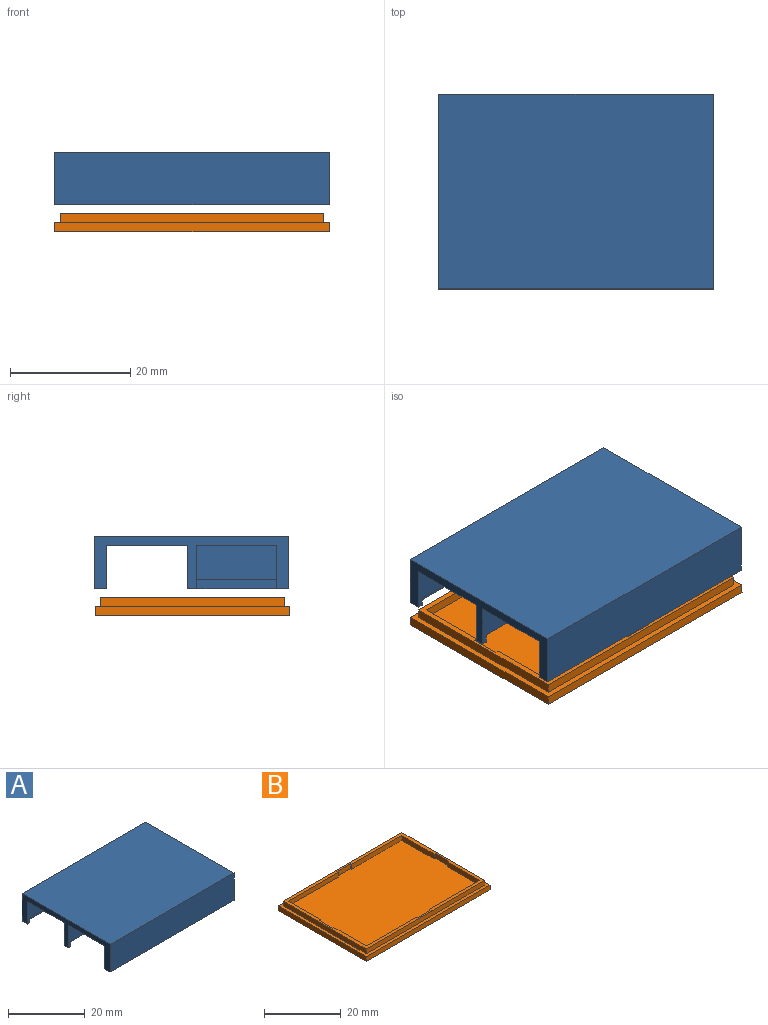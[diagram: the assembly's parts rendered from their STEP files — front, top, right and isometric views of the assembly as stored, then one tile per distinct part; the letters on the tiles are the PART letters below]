
ASSEMBLY  parts=2 mates=1
PART A: 26 faces, bbox 45.6x32.4x8.8 mm
  f0: plane 43.8x15.93mm, normal (0,0,-1), area 64.5mm2, adj f5,f7,f12,f16,f17,f18
  f1: plane 45.6x28.4mm, normal (0,0,-1), area 1227.9mm2, adj f2,f4,f5,f7,f8,f12,f13,f14
  f2: plane 32.4x8.76mm, normal (-1,0,0), area 88.5mm2, adj f1,f6,f7,f8,f9,f11,f13,f14
  f3: plane 24.1x1.5mm, normal (0,0,-1), area 36.1mm2, adj f13,f14,f15,f24
  f4: plane 32.4x8.76mm, normal (1,0,0), area 185.3mm2, adj f1,f6,f8,f9,f11,f12,f19,f23
  f5: plane 14.83x5.76mm, normal (-1,0,0), area 85.4mm2, adj f0,f1,f7,f12
  f6: plane 45.6x8.76mm, normal (0,-1,0), area 399.5mm2, adj f2,f4,f11,f19
  f7: plane 43.6x7.26mm, normal (0,1,0), area 252.5mm2, adj f0,f1,f2,f5,f18,f19
  f8: plane 45.6x7.26mm, normal (0,-1,0), area 265.4mm2, adj f1,f2,f4,f10,f20,f22,f23
  f9: plane 45.6x8.76mm, normal (0,1,0), area 399.5mm2, adj f2,f4,f11,f23
  f10: plane 43.8x1.1mm, normal (0,0,-1), area 48.2mm2, adj f8,f20,f21,f22
  f11: plane 45.6x32.4mm, normal (0,0,1), area 1477.4mm2, adj f2,f4,f6,f9
  f12: plane 7.26x2mm, normal (0,1,0), area 12.9mm2, adj f0,f1,f4,f5,f16,f19
  f13: plane 25x7.26mm, normal (0,1,0), area 145.4mm2, adj f1,f2,f3,f15,f24,f25
  f14: plane 25x7.26mm, normal (0,-1,0), area 145.3mm2, adj f1,f2,f3,f15,f24,f25
  f15: plane 5.76x1.5mm, normal (1,0,0), area 8.6mm2, adj f1,f3,f13,f14
  f16: plane 15.93x1.5mm, normal (-1,0,0), area 23.9mm2, adj f0,f12,f17,f19
  f17: plane 43.8x1.5mm, normal (0,1,0), area 65.7mm2, adj f0,f16,f18,f19
  f18: plane 1.5x1.1mm, normal (1,0,0), area 1.6mm2, adj f0,f7,f17,f19
  f19: plane 45.6x16.83mm, normal (0,0,-1), area 56.4mm2, adj f2,f4,f6,f7,f12,f16,f17,f18
  f20: plane 1.5x1.1mm, normal (1,0,0), area 1.7mm2, adj f8,f10,f21,f23
  f21: plane 43.8x1.5mm, normal (0,-1,0), area 65.7mm2, adj f10,f20,f22,f23
  f22: plane 1.5x1.1mm, normal (-1,0,0), area 1.7mm2, adj f8,f10,f21,f23
  f23: plane 45.6x2mm, normal (0,0,-1), area 43mm2, adj f2,f4,f8,f9,f20,f21,f22
  f24: plane 1.5x1.5mm, normal (1,0,0), area 2.3mm2, adj f3,f13,f14,f25
  f25: plane 1.5x0.9mm, normal (0,0,-1), area 1.4mm2, adj f2,f13,f14,f24
PART B: 32 faces, bbox 45.6x32.4x3 mm
  f0: plane 43.7x30.5mm, normal (0,0,1), area 127.4mm2, adj f1,f2,f3,f4,f11,f12,f13,f14
  f1: plane 43.7x1.51mm, normal (0,-1,0), area 66mm2, adj f0,f2,f4,f5
  f2: plane 30.5x1.51mm, normal (-1,0,0), area 46.1mm2, adj f0,f1,f3,f5
  f3: plane 43.7x1.51mm, normal (0,1,0), area 66mm2, adj f0,f2,f4,f5
  f4: plane 30.5x1.51mm, normal (1,0,0), area 46.1mm2, adj f0,f1,f3,f5
  f5: plane 45.6x32.4mm, normal (0,0,1), area 144.6mm2, adj f1,f2,f3,f4,f7,f8,f9,f10
  f6: plane 45.6x32.4mm, normal (0,0,-1), area 1477.4mm2, adj f7,f8,f9,f10
  f7: plane 45.6x1.53mm, normal (0,1,0), area 69.8mm2, adj f5,f6,f8,f10
  f8: plane 32.4x1.53mm, normal (1,0,0), area 49.6mm2, adj f5,f6,f7,f9
  f9: plane 45.6x1.53mm, normal (0,-1,0), area 69.8mm2, adj f5,f6,f8,f10
  f10: plane 32.4x1.53mm, normal (-1,0,0), area 49.6mm2, adj f5,f6,f7,f9
  f11: plane 1.54x0.5mm, normal (1,0,0), area 0.8mm2, adj f0,f12,f28,f31
  f12: plane 18.4x1.54mm, normal (0,-1,0), area 28.3mm2, adj f0,f11,f13,f31
  f13: plane 11.8x1.54mm, normal (1,0,0), area 18.2mm2, adj f0,f12,f14,f31
  f14: plane 1.54x0.5mm, normal (0,-1,0), area 0.8mm2, adj f0,f13,f15,f31
  f15: plane 5x1.54mm, normal (1,0,0), area 7.7mm2, adj f0,f14,f16,f31
  f16: plane 1.54x0.5mm, normal (0,1,0), area 0.8mm2, adj f0,f15,f17,f31
  f17: plane 11.8x1.54mm, normal (1,0,0), area 18.2mm2, adj f0,f16,f18,f31
  f18: plane 18.4x1.54mm, normal (0,1,0), area 28.3mm2, adj f0,f17,f19,f31
  f19: plane 1.54x0.5mm, normal (1,0,0), area 0.8mm2, adj f0,f18,f20,f31
  f20: plane 5x1.54mm, normal (0,1,0), area 7.7mm2, adj f0,f19,f21,f31
  f21: plane 1.54x0.5mm, normal (-1,0,0), area 0.8mm2, adj f0,f20,f22,f31
  f22: plane 18.4x1.54mm, normal (0,1,0), area 28.3mm2, adj f0,f21,f23,f31
  f23: plane 11.8x1.54mm, normal (-1,0,0), area 18.2mm2, adj f0,f22,f24,f31
  f24: plane 1.54x0.5mm, normal (0,1,0), area 0.8mm2, adj f0,f23,f25,f31
  f25: plane 5x1.54mm, normal (-1,0,0), area 7.7mm2, adj f0,f24,f26,f31
  f26: plane 1.54x0.5mm, normal (0,-1,0), area 0.8mm2, adj f0,f25,f27,f31
  f27: plane 11.8x1.54mm, normal (-1,0,0), area 18.2mm2, adj f0,f26,f29,f31
  f28: plane 5x1.54mm, normal (0,-1,0), area 7.7mm2, adj f0,f11,f30,f31
  f29: plane 18.4x1.54mm, normal (0,-1,0), area 28.3mm2, adj f0,f27,f30,f31
  f30: plane 1.54x0.5mm, normal (-1,0,0), area 0.8mm2, adj f0,f28,f29,f31
  f31: plane 42.8x29.6mm, normal (0,0,1), area 1205.5mm2, adj f11,f12,f13,f14,f15,f16,f17,f18
PLACE A t=(5.52,-4.86,10.47)mm
PLACE B t=(5.75,-4.86,4.47)mm
MATE planar A.f2 <-> B.f10  axis (-1,0,0) through (-17.05,-4.75,15)mm
